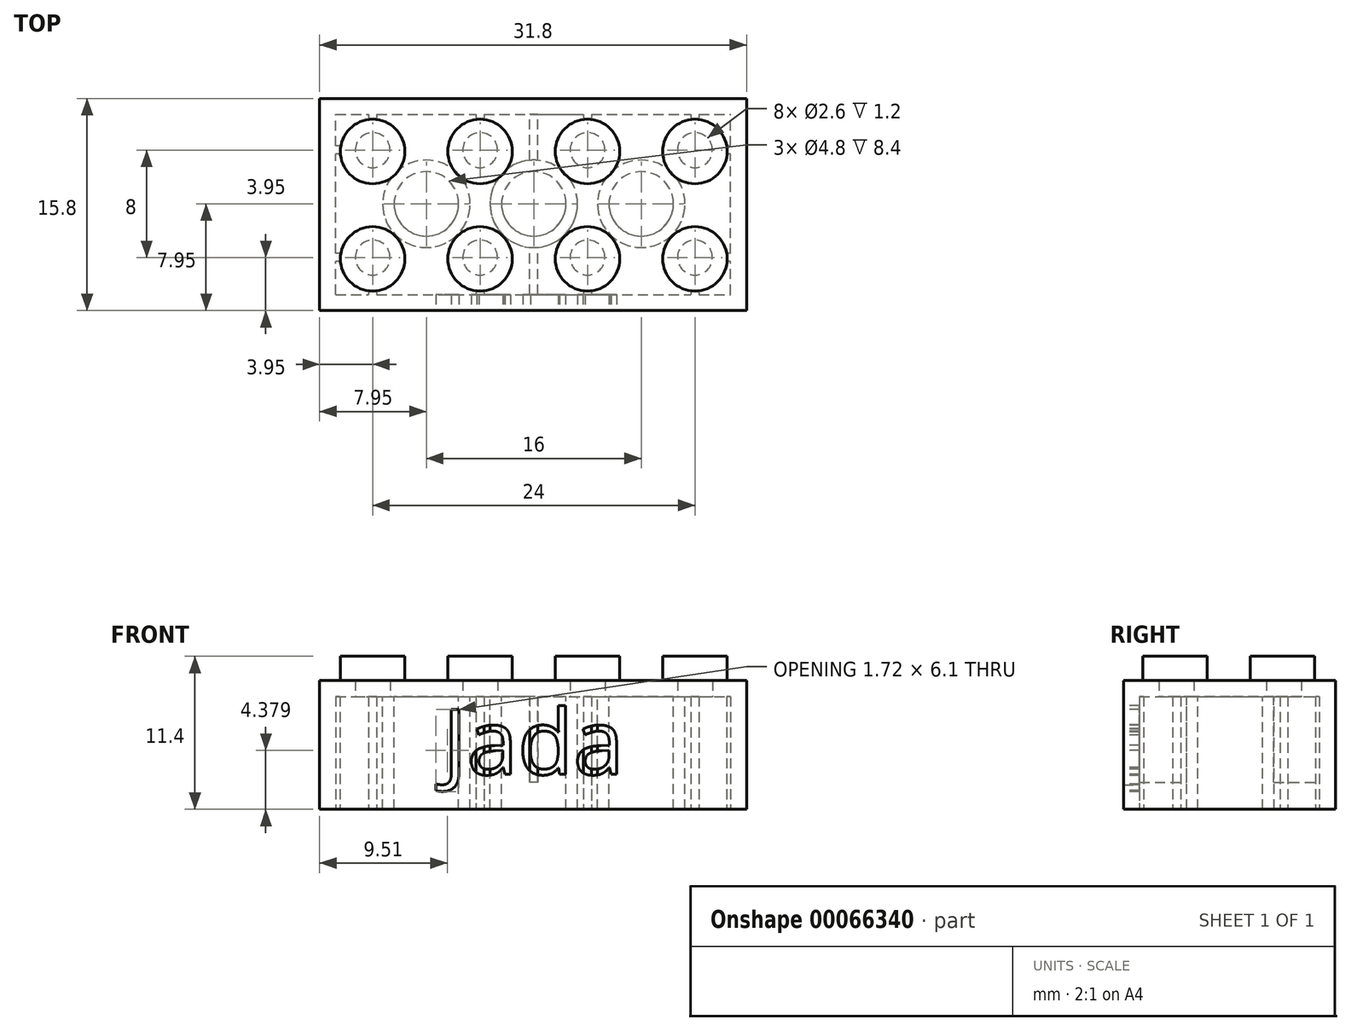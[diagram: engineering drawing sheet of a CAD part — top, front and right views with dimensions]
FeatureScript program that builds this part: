
annotation { "Feature Type Name" : "Feature", "Feature Type Description" : "" }
export const myFeature = defineFeature(function(context is Context, id is Id, definition is map)
    precondition{}
    {
        {
            var Q0;
            Q0=qCreatedBy(makeId("Top.planeOp"),FACE);
            var sketch = newSketch(context, id + "F0", { "sketchPlane" : qUnion([Q0])});
            skLineSegment(sketch, "E0.rect.bottom", {"start": v(15.9, 7.9) * mm, "end": v(-15.9, 7.9) * mm});
            skLineSegment(sketch, "E0.rect.top", {"start": v(15.9, -7.9) * mm, "end": v(-15.9, -7.9) * mm});
            skLineSegment(sketch, "E0.rect.left", {"start": v(15.9, 7.9) * mm, "end": v(15.9, -7.9) * mm});
            skLineSegment(sketch, "E0.rect.right", {"start": v(-15.9, 7.9) * mm, "end": v(-15.9, -7.9) * mm});
            skPoint(sketch, "E0.rect.middle", {"position": v(0, 0) * mm});
            skSolve(sketch);
        }
        {
            var Q0;
            Q0 = qSketchRegion(id + "F0", true);
            extrude(context, id + "F1", {"entities" : qUnion([Q0]), "depth" : 9.6 * mm});
        }
        {
            var Q0;
            Q0=makeQuery(id+"F1.opExtrude","CAP_FACE",FACE,{"disambiguationData":[OSD([sQuery(id+"F0.wireOp",EDGE,"E0.rect.bottom"),sQuery(id+"F0.wireOp",EDGE,"E0.rect.top"),sQuery(id+"F0.wireOp",EDGE,"E0.rect.left"),sQuery(id+"F0.wireOp",EDGE,"E0.rect.right")])],"isStart":true});
            var sketch = newSketch(context, id + "F2", { "sketchPlane" : qUnion([Q0])});
            skLineSegment(sketch, "E1.rect.bottom", {"start": v(-14.7, 6.7) * mm, "end": v(14.7, 6.7) * mm});
            skLineSegment(sketch, "E1.rect.top", {"start": v(-14.7, -6.7) * mm, "end": v(14.7, -6.7) * mm});
            skLineSegment(sketch, "E1.rect.left", {"start": v(-14.7, 6.7) * mm, "end": v(-14.7, -6.7) * mm});
            skLineSegment(sketch, "E1.rect.right", {"start": v(14.7, 6.7) * mm, "end": v(14.7, -6.7) * mm});
            skPoint(sketch, "E1.rect.middle", {"position": v(0, 0) * mm});
            skSolve(sketch);
        }
        {
            var Q0;
            Q0=makeQuery(id+"F2.imprint","IMPRINT",FACE,{"disambiguationData":[TD([[makeQuery(id+"F2.imprint","IMPRINT",EDGE,{"derivedFrom":sQuery(id+"F2.wireOp",EDGE,"E1.rect.bottom")}),-1.0]])]});
            extrude(context, id + "F3", {"entities" : qUnion([Q0]), "operationType" : NewBodyOperationType.REMOVE, "oppositeDirection" : true, "depth" : 8.4 * mm});
        }
        {
            var Q0;
            Q0=makeQuery(id+"F1.opExtrude","CAP_FACE",FACE,{"disambiguationData":[OSD([sQuery(id+"F0.wireOp",EDGE,"E0.rect.bottom"),sQuery(id+"F0.wireOp",EDGE,"E0.rect.top"),sQuery(id+"F0.wireOp",EDGE,"E0.rect.left"),sQuery(id+"F0.wireOp",EDGE,"E0.rect.right")])],"isStart":false});
            var sketch = newSketch(context, id + "F4", { "sketchPlane" : qUnion([Q0])});
            skLineSegment(sketch, "E2", {"start": v(-15.52, 0) * mm, "end": v(15.84, 0) * mm, "construction": true});
            skCircle(sketch, "E3", {"center": v(-11.95, 3.95) * mm, "radius": 2.4 * mm});
            skCircle(sketch, "E4.0.1.0", {"center": v(-11.95, -4.05) * mm, "radius": 2.4 * mm});
            skCircle(sketch, "E4.1.0.0", {"center": v(-3.95, 3.95) * mm, "radius": 2.4 * mm});
            skCircle(sketch, "E4.1.1.0", {"center": v(-3.95, -4.05) * mm, "radius": 2.4 * mm});
            skCircle(sketch, "E4.2.0.0", {"center": v(4.05, 3.95) * mm, "radius": 2.4 * mm});
            skCircle(sketch, "E4.2.1.0", {"center": v(4.05, -4.05) * mm, "radius": 2.4 * mm});
            skCircle(sketch, "E4.3.0.0", {"center": v(12.05, 3.95) * mm, "radius": 2.4 * mm});
            skCircle(sketch, "E4.3.1.0", {"center": v(12.05, -4.05) * mm, "radius": 2.4 * mm});
            skLineSegment(sketch, "E4.direction1", {"start": v(-11.95, 3.95) * mm, "end": v(-3.95, 3.95) * mm, "construction": true});
            skLineSegment(sketch, "E4.direction2", {"start": v(-11.95, 3.95) * mm, "end": v(-11.95, -4.05) * mm, "construction": true});
            skSolve(sketch);
        }
        {
            var Q0;
            Q0 = qSketchRegion(id + "F4", true);
            extrude(context, id + "F5", {"entities" : qUnion([Q0]), "operationType" : NewBodyOperationType.ADD, "depth" : 1.8 * mm});
        }
        {
            var Q0;
            Q0=makeQuery(id+"F3.boolean.opBoolean","COPY",FACE,{"derivedFrom":makeQuery(id+"F3.opExtrude","CAP_FACE",FACE,{"disambiguationData":[OSD([sQuery(id+"F2.wireOp",EDGE,"E1.rect.bottom"),sQuery(id+"F2.wireOp",EDGE,"E1.rect.top"),sQuery(id+"F2.wireOp",EDGE,"E1.rect.left"),sQuery(id+"F2.wireOp",EDGE,"E1.rect.right")])],"isStart":false})});
            var sketch = newSketch(context, id + "F6", { "sketchPlane" : qUnion([Q0])});
            skCircle(sketch, "E5", {"center": v(-11.95, 3.95) * mm, "radius": 1.3 * mm});
            skCircle(sketch, "E6.0.1.0", {"center": v(-11.95, -4.05) * mm, "radius": 1.3 * mm});
            skCircle(sketch, "E6.1.0.0", {"center": v(-3.95, 3.95) * mm, "radius": 1.3 * mm});
            skCircle(sketch, "E6.1.1.0", {"center": v(-3.95, -4.05) * mm, "radius": 1.3 * mm});
            skCircle(sketch, "E6.2.0.0", {"center": v(4.05, 3.95) * mm, "radius": 1.3 * mm});
            skCircle(sketch, "E6.2.1.0", {"center": v(4.05, -4.05) * mm, "radius": 1.3 * mm});
            skCircle(sketch, "E6.3.0.0", {"center": v(12.05, 3.95) * mm, "radius": 1.3 * mm});
            skCircle(sketch, "E6.3.1.0", {"center": v(12.05, -4.05) * mm, "radius": 1.3 * mm});
            skLineSegment(sketch, "E6.direction1", {"start": v(-11.95, 3.95) * mm, "end": v(-3.95, 3.95) * mm, "construction": true});
            skLineSegment(sketch, "E6.direction2", {"start": v(-11.95, 3.95) * mm, "end": v(-11.95, -4.05) * mm, "construction": true});
            skPoint(sketch, "E7", {"position": v(-28.03, 9.77) * mm});
            skSolve(sketch);
        }
        {
            var Q0;
            Q0 = qSketchRegion(id + "F6", true);
            extrude(context, id + "F7", {"entities" : qUnion([Q0]), "operationType" : NewBodyOperationType.REMOVE, "oppositeDirection" : true, "depth" : 1.2 * mm});
        }
        {
            var Q0;
            Q0=makeQuery(id+"F3.boolean.opBoolean","COPY",FACE,{"derivedFrom":makeQuery(id+"F3.opExtrude","CAP_FACE",FACE,{"disambiguationData":[OSD([sQuery(id+"F2.wireOp",EDGE,"E1.rect.bottom"),sQuery(id+"F2.wireOp",EDGE,"E1.rect.top"),sQuery(id+"F2.wireOp",EDGE,"E1.rect.left"),sQuery(id+"F2.wireOp",EDGE,"E1.rect.right")])],"isStart":false})});
            var sketch = newSketch(context, id + "F8", { "sketchPlane" : qUnion([Q0])});
            skLineSegment(sketch, "E8", {"start": v(-11.95, 3.95) * mm, "end": v(-3.95, -4.05) * mm, "construction": true});
            skLineSegment(sketch, "E9", {"start": v(-3.95, 3.95) * mm, "end": v(-11.95, -4.05) * mm, "construction": true});
            skLineSegment(sketch, "E10", {"start": v(-3.95, -4.05) * mm, "end": v(4.05, 3.95) * mm, "construction": true});
            skLineSegment(sketch, "E11", {"start": v(4.05, 3.95) * mm, "end": v(12.05, -4.05) * mm, "construction": true});
            skLineSegment(sketch, "E12", {"start": v(-3.95, 3.95) * mm, "end": v(4.05, -4.05) * mm, "construction": true});
            skLineSegment(sketch, "E13", {"start": v(4.05, -4.05) * mm, "end": v(12.05, 3.95) * mm, "construction": true});
            skCircle(sketch, "E14", {"center": v(-7.95, -0.05) * mm, "radius": 3.25 * mm});
            skCircle(sketch, "E15", {"center": v(0.05, -0.05) * mm, "radius": 3.25 * mm});
            skCircle(sketch, "E16", {"center": v(8.05, -0.05) * mm, "radius": 3.25 * mm});
            skCircle(sketch, "E17", {"center": v(-7.95, -0.05) * mm, "radius": 2.4 * mm});
            skCircle(sketch, "E18", {"center": v(8.05, -0.05) * mm, "radius": 2.4 * mm});
            skCircle(sketch, "E19", {"center": v(0.05, -0.05) * mm, "radius": 2.4 * mm});
            skSolve(sketch);
        }
        {
            var Q0;
            Q0 = qSketchRegion(id + "F8", true);
            var Q1;
            Q1=makeQuery(id+"F1.opExtrude","CAP_FACE",FACE,{"disambiguationData":[OSD([sQuery(id+"F0.wireOp",EDGE,"E0.rect.bottom"),sQuery(id+"F0.wireOp",EDGE,"E0.rect.top"),sQuery(id+"F0.wireOp",EDGE,"E0.rect.left"),sQuery(id+"F0.wireOp",EDGE,"E0.rect.right")])],"isStart":true});
            extrude(context, id + "F9", {"entities" : qUnion([Q0]), "operationType" : NewBodyOperationType.ADD, "endBound" : BoundingType.UP_TO_SURFACE, "endBoundEntityFace" : qUnion([Q1]), "depth" : 25 * mm});
        }
        {
            var Q0;
            Q0=makeQuery(id+"F1.opExtrude","CAP_FACE",FACE,{"disambiguationData":[OSD([sQuery(id+"F0.wireOp",EDGE,"E0.rect.bottom"),sQuery(id+"F0.wireOp",EDGE,"E0.rect.top"),sQuery(id+"F0.wireOp",EDGE,"E0.rect.left"),sQuery(id+"F0.wireOp",EDGE,"E0.rect.right")])],"isStart":true});
            var sketch = newSketch(context, id + "F10", { "sketchPlane" : qUnion([Q0])});
            skLineSegment(sketch, "E20.bottom", {"start": v(-12.25, 6.7) * mm, "end": v(-11.65, 6.7) * mm});
            skLineSegment(sketch, "E20.top", {"start": v(-12.25, 6.4) * mm, "end": v(-11.65, 6.4) * mm});
            skLineSegment(sketch, "E20.left", {"start": v(-12.25, 6.7) * mm, "end": v(-12.25, 6.4) * mm});
            skLineSegment(sketch, "E20.right", {"start": v(-11.65, 6.7) * mm, "end": v(-11.65, 6.4) * mm});
            skLineSegment(sketch, "E21", {"start": v(-11.95, 13.16) * mm, "end": v(-11.95, -4.05) * mm, "construction": true});
            skLineSegment(sketch, "E22.0.1.0", {"start": v(-12.25, -6.7) * mm, "end": v(-11.65, -6.7) * mm});
            skLineSegment(sketch, "E22.0.1.1", {"start": v(-12.25, -6.4) * mm, "end": v(-11.65, -6.4) * mm});
            skLineSegment(sketch, "E22.0.1.2", {"start": v(-12.25, -6.4) * mm, "end": v(-12.25, -6.7) * mm});
            skLineSegment(sketch, "E22.0.1.3", {"start": v(-11.65, -6.4) * mm, "end": v(-11.65, -6.7) * mm});
            skLineSegment(sketch, "E22.1.0.0", {"start": v(-4.25, 6.4) * mm, "end": v(-3.65, 6.4) * mm});
            skLineSegment(sketch, "E22.1.0.1", {"start": v(-4.25, 6.7) * mm, "end": v(-3.65, 6.7) * mm});
            skLineSegment(sketch, "E22.1.0.2", {"start": v(-4.25, 6.7) * mm, "end": v(-4.25, 6.4) * mm});
            skLineSegment(sketch, "E22.1.0.3", {"start": v(-3.65, 6.7) * mm, "end": v(-3.65, 6.4) * mm});
            skLineSegment(sketch, "E22.1.1.0", {"start": v(-4.25, -6.7) * mm, "end": v(-3.65, -6.7) * mm});
            skLineSegment(sketch, "E22.1.1.1", {"start": v(-4.25, -6.4) * mm, "end": v(-3.65, -6.4) * mm});
            skLineSegment(sketch, "E22.1.1.2", {"start": v(-4.25, -6.4) * mm, "end": v(-4.25, -6.7) * mm});
            skLineSegment(sketch, "E22.1.1.3", {"start": v(-3.65, -6.4) * mm, "end": v(-3.65, -6.7) * mm});
            skLineSegment(sketch, "E22.2.0.0", {"start": v(3.75, 6.4) * mm, "end": v(4.35, 6.4) * mm});
            skLineSegment(sketch, "E22.2.0.1", {"start": v(3.75, 6.7) * mm, "end": v(4.35, 6.7) * mm});
            skLineSegment(sketch, "E22.2.0.2", {"start": v(3.75, 6.7) * mm, "end": v(3.75, 6.4) * mm});
            skLineSegment(sketch, "E22.2.0.3", {"start": v(4.35, 6.7) * mm, "end": v(4.35, 6.4) * mm});
            skLineSegment(sketch, "E22.2.1.0", {"start": v(3.75, -6.7) * mm, "end": v(4.35, -6.7) * mm});
            skLineSegment(sketch, "E22.2.1.1", {"start": v(3.75, -6.4) * mm, "end": v(4.35, -6.4) * mm});
            skLineSegment(sketch, "E22.2.1.2", {"start": v(3.75, -6.4) * mm, "end": v(3.75, -6.7) * mm});
            skLineSegment(sketch, "E22.2.1.3", {"start": v(4.35, -6.4) * mm, "end": v(4.35, -6.7) * mm});
            skLineSegment(sketch, "E22.3.0.0", {"start": v(11.75, 6.4) * mm, "end": v(12.35, 6.4) * mm});
            skLineSegment(sketch, "E22.3.0.1", {"start": v(11.75, 6.7) * mm, "end": v(12.35, 6.7) * mm});
            skLineSegment(sketch, "E22.3.0.2", {"start": v(11.75, 6.7) * mm, "end": v(11.75, 6.4) * mm});
            skLineSegment(sketch, "E22.3.0.3", {"start": v(12.35, 6.7) * mm, "end": v(12.35, 6.4) * mm});
            skLineSegment(sketch, "E22.3.1.0", {"start": v(11.75, -6.7) * mm, "end": v(12.35, -6.7) * mm});
            skLineSegment(sketch, "E22.3.1.1", {"start": v(11.75, -6.4) * mm, "end": v(12.35, -6.4) * mm});
            skLineSegment(sketch, "E22.3.1.2", {"start": v(11.75, -6.4) * mm, "end": v(11.75, -6.7) * mm});
            skLineSegment(sketch, "E22.3.1.3", {"start": v(12.35, -6.4) * mm, "end": v(12.35, -6.7) * mm});
            skLineSegment(sketch, "E22.direction1", {"start": v(-12.25, 6.4) * mm, "end": v(-4.25, 6.4) * mm, "construction": true});
            skLineSegment(sketch, "E22.direction2", {"start": v(-12.25, 6.4) * mm, "end": v(-12.25, -6.7) * mm, "construction": true});
            skSolve(sketch);
        }
        {
            var Q0;
            Q0 = qSketchRegion(id + "F10", true);
            var Q1;
            {var subQ0=sQuery(id+"F2.wireOp",EDGE,"E1.rect.bottom");var subQ1=sQuery(id+"F2.wireOp",EDGE,"E1.rect.top");var subQ2=sQuery(id+"F2.wireOp",EDGE,"E1.rect.left");var subQ3=sQuery(id+"F2.wireOp",EDGE,"E1.rect.right");Q1=makeQuery(id+"F9.boolean.opBoolean","SPLIT",FACE,{"disambiguationData":[TD([makeQuery(id+"F3.boolean.opBoolean","COPY",FACE,{"derivedFrom":makeQuery(id+"F3.opExtrude","SWEPT_FACE",FACE,{"disambiguationData":[OSD([subQ0])]})})])],"derivedFrom":makeQuery(id+"F3.boolean.opBoolean","COPY",FACE,{"derivedFrom":makeQuery(id+"F3.opExtrude","CAP_FACE",FACE,{"disambiguationData":[OSD([subQ0,subQ1,subQ2,subQ3])],"isStart":false})})});}
            extrude(context, id + "F11", {"entities" : qUnion([Q0]), "operationType" : NewBodyOperationType.ADD, "endBound" : BoundingType.UP_TO_SURFACE, "oppositeDirection" : true, "endBoundEntityFace" : qUnion([Q1]), "depth" : 25 * mm});
        }
        {
            var Q0;
            Q0=makeQuery(id+"F11.boolean.opBoolean","MERGE",FACE,{"derivedFrom":[makeQuery(id+"F1.opExtrude","CAP_FACE",FACE,{"disambiguationData":[OSD([sQuery(id+"F0.wireOp",EDGE,"E0.rect.bottom"),sQuery(id+"F0.wireOp",EDGE,"E0.rect.top"),sQuery(id+"F0.wireOp",EDGE,"E0.rect.left"),sQuery(id+"F0.wireOp",EDGE,"E0.rect.right")])],"isStart":true}),makeQuery(id+"F11.opExtrude","CAP_FACE",FACE,{"disambiguationData":[OSD([sQuery(id+"F10.wireOp",EDGE,"E20.bottom"),sQuery(id+"F10.wireOp",EDGE,"E20.top"),sQuery(id+"F10.wireOp",EDGE,"E20.left"),sQuery(id+"F10.wireOp",EDGE,"E20.right")])],"isStart":true}),makeQuery(id+"F11.opExtrude","CAP_FACE",FACE,{"disambiguationData":[OSD([sQuery(id+"F10.wireOp",EDGE,"E22.0.1.0"),sQuery(id+"F10.wireOp",EDGE,"E22.0.1.1"),sQuery(id+"F10.wireOp",EDGE,"E22.0.1.2"),sQuery(id+"F10.wireOp",EDGE,"E22.0.1.3")])],"isStart":true}),makeQuery(id+"F11.opExtrude","CAP_FACE",FACE,{"disambiguationData":[OSD([sQuery(id+"F10.wireOp",EDGE,"E22.1.0.0"),sQuery(id+"F10.wireOp",EDGE,"E22.1.0.1"),sQuery(id+"F10.wireOp",EDGE,"E22.1.0.2"),sQuery(id+"F10.wireOp",EDGE,"E22.1.0.3")])],"isStart":true}),makeQuery(id+"F11.opExtrude","CAP_FACE",FACE,{"disambiguationData":[OSD([sQuery(id+"F10.wireOp",EDGE,"E22.1.1.0"),sQuery(id+"F10.wireOp",EDGE,"E22.1.1.1"),sQuery(id+"F10.wireOp",EDGE,"E22.1.1.2"),sQuery(id+"F10.wireOp",EDGE,"E22.1.1.3")])],"isStart":true}),makeQuery(id+"F11.opExtrude","CAP_FACE",FACE,{"disambiguationData":[OSD([sQuery(id+"F10.wireOp",EDGE,"E22.2.0.0"),sQuery(id+"F10.wireOp",EDGE,"E22.2.0.1"),sQuery(id+"F10.wireOp",EDGE,"E22.2.0.2"),sQuery(id+"F10.wireOp",EDGE,"E22.2.0.3")])],"isStart":true}),makeQuery(id+"F11.opExtrude","CAP_FACE",FACE,{"disambiguationData":[OSD([sQuery(id+"F10.wireOp",EDGE,"E22.2.1.0"),sQuery(id+"F10.wireOp",EDGE,"E22.2.1.1"),sQuery(id+"F10.wireOp",EDGE,"E22.2.1.2"),sQuery(id+"F10.wireOp",EDGE,"E22.2.1.3")])],"isStart":true}),makeQuery(id+"F11.opExtrude","CAP_FACE",FACE,{"disambiguationData":[OSD([sQuery(id+"F10.wireOp",EDGE,"E22.3.0.0"),sQuery(id+"F10.wireOp",EDGE,"E22.3.0.1"),sQuery(id+"F10.wireOp",EDGE,"E22.3.0.2"),sQuery(id+"F10.wireOp",EDGE,"E22.3.0.3")])],"isStart":true}),makeQuery(id+"F11.opExtrude","CAP_FACE",FACE,{"disambiguationData":[OSD([sQuery(id+"F10.wireOp",EDGE,"E22.3.1.0"),sQuery(id+"F10.wireOp",EDGE,"E22.3.1.1"),sQuery(id+"F10.wireOp",EDGE,"E22.3.1.2"),sQuery(id+"F10.wireOp",EDGE,"E22.3.1.3")])],"isStart":true})]});
            var sketch = newSketch(context, id + "F12", { "sketchPlane" : qUnion([Q0])});
            skLineSegment(sketch, "E23", {"start": v(-15.9, 3.95) * mm, "end": v(-3.95, 3.95) * mm, "construction": true});
            skLineSegment(sketch, "E24.bottom", {"start": v(-14.7, 4.25) * mm, "end": v(-14.4, 4.25) * mm});
            skLineSegment(sketch, "E24.top", {"start": v(-14.7, 3.65) * mm, "end": v(-14.4, 3.65) * mm});
            skLineSegment(sketch, "E24.left", {"start": v(-14.7, 4.25) * mm, "end": v(-14.7, 3.65) * mm});
            skLineSegment(sketch, "E24.right", {"start": v(-14.4, 4.25) * mm, "end": v(-14.4, 3.65) * mm});
            skLineSegment(sketch, "E25.0.1.0", {"start": v(-14.7, -3.75) * mm, "end": v(-14.4, -3.75) * mm});
            skLineSegment(sketch, "E25.0.1.1", {"start": v(-14.7, -3.75) * mm, "end": v(-14.7, -4.35) * mm});
            skLineSegment(sketch, "E25.0.1.2", {"start": v(-14.7, -4.35) * mm, "end": v(-14.4, -4.35) * mm});
            skLineSegment(sketch, "E25.0.1.3", {"start": v(-14.4, -3.75) * mm, "end": v(-14.4, -4.35) * mm});
            skLineSegment(sketch, "E25.1.0.0", {"start": v(14.4, 4.25) * mm, "end": v(14.7, 4.25) * mm});
            skLineSegment(sketch, "E25.1.0.1", {"start": v(14.4, 4.25) * mm, "end": v(14.4, 3.65) * mm});
            skLineSegment(sketch, "E25.1.0.2", {"start": v(14.4, 3.65) * mm, "end": v(14.7, 3.65) * mm});
            skLineSegment(sketch, "E25.1.0.3", {"start": v(14.7, 4.25) * mm, "end": v(14.7, 3.65) * mm});
            skLineSegment(sketch, "E25.1.1.0", {"start": v(14.4, -3.75) * mm, "end": v(14.7, -3.75) * mm});
            skLineSegment(sketch, "E25.1.1.1", {"start": v(14.4, -3.75) * mm, "end": v(14.4, -4.35) * mm});
            skLineSegment(sketch, "E25.1.1.2", {"start": v(14.4, -4.35) * mm, "end": v(14.7, -4.35) * mm});
            skLineSegment(sketch, "E25.1.1.3", {"start": v(14.7, -3.75) * mm, "end": v(14.7, -4.35) * mm});
            skLineSegment(sketch, "E25.direction2", {"start": v(-14.7, 4.25) * mm, "end": v(-14.7, -3.75) * mm, "construction": true});
            skSolve(sketch);
        }
        {
            var Q0;
            Q0 = qSketchRegion(id + "F12", true);
            var Q1;
            {var subQ0=sQuery(id+"F2.wireOp",EDGE,"E1.rect.bottom");var subQ1=sQuery(id+"F2.wireOp",EDGE,"E1.rect.top");var subQ2=sQuery(id+"F2.wireOp",EDGE,"E1.rect.left");var subQ3=sQuery(id+"F2.wireOp",EDGE,"E1.rect.right");Q1=makeQuery(id+"F9.boolean.opBoolean","SPLIT",FACE,{"disambiguationData":[TD([makeQuery(id+"F3.boolean.opBoolean","COPY",FACE,{"derivedFrom":makeQuery(id+"F3.opExtrude","SWEPT_FACE",FACE,{"disambiguationData":[OSD([subQ0])]})})])],"derivedFrom":makeQuery(id+"F3.boolean.opBoolean","COPY",FACE,{"derivedFrom":makeQuery(id+"F3.opExtrude","CAP_FACE",FACE,{"disambiguationData":[OSD([subQ0,subQ1,subQ2,subQ3])],"isStart":false})})});}
            extrude(context, id + "F13", {"entities" : qUnion([Q0]), "operationType" : NewBodyOperationType.ADD, "endBound" : BoundingType.UP_TO_SURFACE, "oppositeDirection" : true, "endBoundEntityFace" : qUnion([Q1]), "depth" : 25 * mm});
        }
        {
            var Q0;
            Q0=makeQuery(id+"F8.imprint","IMPRINT",FACE,{"disambiguationData":[TD([[makeQuery(id+"F8.imprint","IMPRINT",EDGE,{"derivedFrom":sQuery(id+"F8.wireOp",EDGE,"E14")}),-1.0]])]});
            var sketch = newSketch(context, id + "F14", { "sketchPlane" : qUnion([Q0])});
            skLineSegment(sketch, "E26.bottom", {"start": v(-0.25, 6.96) * mm, "end": v(0.35, 6.96) * mm});
            skLineSegment(sketch, "E26.top", {"start": v(-0.25, 2.96) * mm, "end": v(0.35, 2.96) * mm});
            skLineSegment(sketch, "E26.left", {"start": v(-0.25, 6.96) * mm, "end": v(-0.25, 2.96) * mm});
            skLineSegment(sketch, "E26.right", {"start": v(0.35, 6.96) * mm, "end": v(0.35, 2.96) * mm});
            skSolve(sketch);
        }
        {
            var Q0;
            Q0 = qSketchRegion(id + "F14", true);
            extrude(context, id + "F15", {"entities" : qUnion([Q0]), "operationType" : NewBodyOperationType.ADD, "depth" : 6.4 * mm});
        }
        {
            var Q0;
            {var subQ0=sQuery(id+"F2.wireOp",EDGE,"E1.rect.bottom");var subQ1=sQuery(id+"F2.wireOp",EDGE,"E1.rect.top");var subQ2=sQuery(id+"F2.wireOp",EDGE,"E1.rect.left");var subQ3=sQuery(id+"F2.wireOp",EDGE,"E1.rect.right");Q0=makeQuery(id+"F9.boolean.opBoolean","SPLIT",FACE,{"disambiguationData":[TD([makeQuery(id+"F3.boolean.opBoolean","COPY",FACE,{"derivedFrom":makeQuery(id+"F3.opExtrude","SWEPT_FACE",FACE,{"disambiguationData":[OSD([subQ0])]})})])],"derivedFrom":makeQuery(id+"F3.boolean.opBoolean","COPY",FACE,{"derivedFrom":makeQuery(id+"F3.opExtrude","CAP_FACE",FACE,{"disambiguationData":[OSD([subQ0,subQ1,subQ2,subQ3])],"isStart":false})})});}
            var sketch = newSketch(context, id + "F16", { "sketchPlane" : qUnion([Q0])});
            skLineSegment(sketch, "E27.bottom", {"start": v(-0.25, -3.1) * mm, "end": v(0.35, -3.1) * mm});
            skLineSegment(sketch, "E27.top", {"start": v(-0.25, -7.1) * mm, "end": v(0.35, -7.1) * mm});
            skLineSegment(sketch, "E27.left", {"start": v(-0.25, -3.1) * mm, "end": v(-0.25, -7.1) * mm});
            skLineSegment(sketch, "E27.right", {"start": v(0.35, -3.1) * mm, "end": v(0.35, -7.1) * mm});
            skSolve(sketch);
        }
        {
            var Q0;
            Q0 = qSketchRegion(id + "F16", true);
            extrude(context, id + "F17", {"entities" : qUnion([Q0]), "operationType" : NewBodyOperationType.ADD, "depth" : 6.4 * mm});
        }
        {
            var Q0;
            Q0=makeQuery(id+"F1.opExtrude","SWEPT_FACE",FACE,{"disambiguationData":[OSD([sQuery(id+"F0.wireOp",EDGE,"E0.rect.top")])]});
            var sketch = newSketch(context, id + "F18", { "sketchPlane" : qUnion([Q0])});
            skText(sketch, "E28", { "text": "Jada", "fontName": "OpenSans-Regular.ttf"});
            skLineSegment(sketch, "E29", {"start": v(0, -1.12) * mm, "end": v(0, 10.67) * mm, "construction": true});
            const initialGuessF18  = {"E28": [-0.00672, 0.0026, 1, 0, 0.00487]};
            skSetInitialGuess(sketch, initialGuessF18);
            skSolve(sketch);
        }
        {
            var Q0;
            Q0 = qSketchRegion(id + "F18", true);
            extrude(context, id + "F19", {"entities" : qUnion([Q0]), "operationType" : NewBodyOperationType.REMOVE, "oppositeDirection" : true, "depth" : 1.2 * mm});
        }
    });
